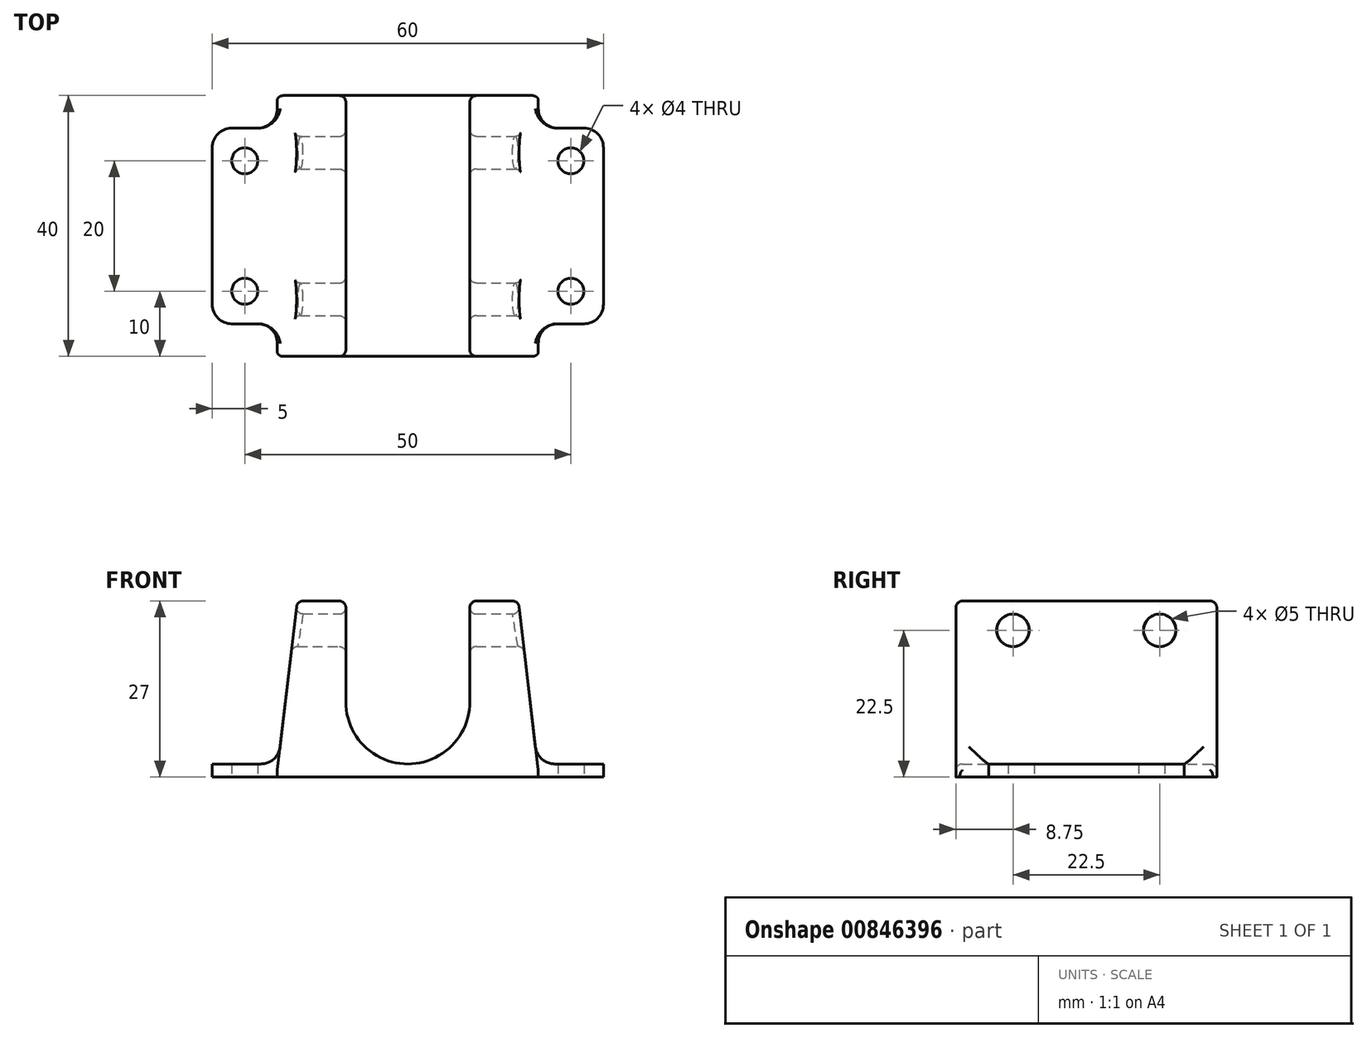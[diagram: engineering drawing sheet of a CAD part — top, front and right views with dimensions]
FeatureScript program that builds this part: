
annotation { "Feature Type Name" : "Feature", "Feature Type Description" : "" }
export const myFeature = defineFeature(function(context is Context, id is Id, definition is map)
    precondition{}
    {
        {
            var Q0;
            Q0=qCreatedBy(makeId("Front.planeOp"),FACE);
            var sketch = newSketch(context, id + "F0", { "sketchPlane" : qUnion([Q0])});
            skLineSegment(sketch, "E0.bottom", {"start": v(0, 0) * mm, "end": v(-20, 0) * mm});
            skLineSegment(sketch, "E0.right", {"start": v(-20, 0) * mm, "end": v(-20, 1) * mm});
            skArc(sketch, "E1", {"start": v(-9.5, 11.56) * mm, "mid": v(-6.74, 4.8) * mm, "end": v(0, 2) * mm});
            skLineSegment(sketch, "E2", {"start": v(-16.95, 27) * mm, "end": v(-20, 1) * mm});
            skLineSegment(sketch, "E3", {"start": v(-9.5, 11.56) * mm, "end": v(-9.5, 27) * mm});
            skPoint(sketch, "E4.end.orphan", {"position": v(-10, 27) * mm});
            skLineSegment(sketch, "E5", {"start": v(-16.95, 27) * mm, "end": v(-9.5, 27) * mm});
            skLineSegment(sketch, "E6.MirrorCS", {"start": v(16.95, 27) * mm, "end": v(20, 1) * mm});
            skLineSegment(sketch, "E7.MirrorCS", {"start": v(16.95, 27) * mm, "end": v(9.5, 27) * mm});
            skLineSegment(sketch, "E8.MirrorCS", {"start": v(9.5, 11.56) * mm, "end": v(9.5, 27) * mm});
            skArc(sketch, "E9.MirrorCS", {"start": v(9.5, 11.56) * mm, "mid": v(6.74, 4.8) * mm, "end": v(0, 2) * mm});
            skLineSegment(sketch, "E10.MirrorCS", {"start": v(0, 0) * mm, "end": v(20, 0) * mm});
            skLineSegment(sketch, "E11.MirrorCS", {"start": v(20, 0) * mm, "end": v(20, 1) * mm});
            skSolve(sketch);
        }
        {
            var Q0;
            Q0 = qSketchRegion(id + "F0", true);
            extrude(context, id + "F1", {"entities" : qUnion([Q0]), "endBound" : BoundingType.SYMMETRIC, "depth" : 40 * mm, "offsetDistance" : 25 * mm});
        }
        {
            var Q0;
            Q0=qCreatedBy(makeId("Right.planeOp"),FACE);
            var sketch = newSketch(context, id + "F2", { "sketchPlane" : qUnion([Q0])});
            skCircle(sketch, "E12", {"center": v(11.25, 22.5) * mm, "radius": 2.5 * mm});
            skCircle(sketch, "E13", {"center": v(-11.25, 22.5) * mm, "radius": 2.5 * mm});
            skSolve(sketch);
        }
        {
            var Q0;
            Q0 = qSketchRegion(id + "F2", true);
            extrude(context, id + "F3", {"entities" : qUnion([Q0]), "operationType" : NewBodyOperationType.REMOVE, "endBound" : BoundingType.SYMMETRIC, "oppositeDirection" : true, "depth" : 40 * mm, "offsetDistance" : 25 * mm});
        }
        {
            var Q0;
            Q0=makeQuery(id+"F1.opExtrude","SWEPT_FACE",FACE,{"disambiguationData":[OSD([sQuery(id+"F0.wireOp",EDGE,"E5")])]});
            var Q1;
            Q1=makeQuery(id+"F1.opExtrude","SWEPT_FACE",FACE,{"disambiguationData":[OSD([sQuery(id+"F0.wireOp",EDGE,"E7.MirrorCS")])]});
            var Q2;
            Q2=makeQuery(id+"F1.opExtrude","CAP_EDGE",EDGE,{"disambiguationData":[OSD([sQuery(id+"F0.wireOp",EDGE,"E6.MirrorCS")])],"isStart":false});
            var Q3;
            Q3=makeQuery(id+"F1.opExtrude","CAP_EDGE",EDGE,{"disambiguationData":[OSD([sQuery(id+"F0.wireOp",EDGE,"E6.MirrorCS")])],"isStart":true});
            var Q4;
            Q4=makeQuery(id+"F1.opExtrude","CAP_EDGE",EDGE,{"disambiguationData":[OSD([sQuery(id+"F0.wireOp",EDGE,"E2")])],"isStart":true});
            var Q5;
            Q5=makeQuery(id+"F1.opExtrude","CAP_EDGE",EDGE,{"disambiguationData":[OSD([sQuery(id+"F0.wireOp",EDGE,"E2")])],"isStart":false});
            var Q6;
            Q6=makeQuery(id+"F1.opExtrude","SWEPT_FACE",FACE,{"disambiguationData":[OSD([sQuery(id+"F0.wireOp",EDGE,"E1"),sQuery(id+"F0.wireOp",EDGE,"E9.MirrorCS")])]});
            var Q7;
            Q7=makeQuery(id+"F1.opExtrude","SWEPT_FACE",FACE,{"disambiguationData":[OSD([sQuery(id+"F0.wireOp",EDGE,"E8.MirrorCS")])]});
            var Q8;
            Q8=makeQuery(id+"F1.opExtrude","SWEPT_FACE",FACE,{"disambiguationData":[OSD([sQuery(id+"F0.wireOp",EDGE,"E3")])]});
            var Q9;
            Q9=makeQuery(id+"F1.opExtrude","SWEPT_FACE",FACE,{"disambiguationData":[OSD([sQuery(id+"F0.wireOp",EDGE,"E2")])]});
            var Q10;
            Q10=makeQuery(id+"F1.opExtrude","SWEPT_FACE",FACE,{"disambiguationData":[OSD([sQuery(id+"F0.wireOp",EDGE,"E6.MirrorCS")])]});
            fillet(context, id + "F4", {"entities" : qUnion([Q0, Q1, Q2, Q3, Q4, Q5, Q6, Q7, Q8, Q9, Q10]), "radius" : 1 * mm, "tangentPropagation" : true, "allowEdgeOverflow" : false});
        }
        {
            var Q0;
            Q0=makeQuery(id+"F1.opExtrude","SWEPT_FACE",FACE,{"disambiguationData":[OSD([sQuery(id+"F0.wireOp",EDGE,"E0.bottom"),sQuery(id+"F0.wireOp",EDGE,"E10.MirrorCS")])]});
            var sketch = newSketch(context, id + "F5", { "sketchPlane" : qUnion([Q0])});
            skLineSegment(sketch, "E14.bottom", {"start": v(-30, 15) * mm, "end": v(30, 15) * mm});
            skLineSegment(sketch, "E14.top", {"start": v(-30, -15) * mm, "end": v(30, -15) * mm});
            skLineSegment(sketch, "E14.left", {"start": v(-30, 15) * mm, "end": v(-30, -15) * mm});
            skLineSegment(sketch, "E14.right", {"start": v(30, 15) * mm, "end": v(30, -15) * mm});
            skCircle(sketch, "E15", {"center": v(-25, 10) * mm, "radius": 2 * mm});
            skCircle(sketch, "E16.0.1.0", {"center": v(-25, -10) * mm, "radius": 2 * mm});
            skCircle(sketch, "E16.1.0.0", {"center": v(25, 10) * mm, "radius": 2 * mm});
            skCircle(sketch, "E16.1.1.0", {"center": v(25, -10) * mm, "radius": 2 * mm});
            skLineSegment(sketch, "E16.direction1", {"start": v(-25, 10) * mm, "end": v(25, 10) * mm, "construction": true});
            skLineSegment(sketch, "E16.direction2", {"start": v(-25, 10) * mm, "end": v(-25, -10) * mm, "construction": true});
            skSolve(sketch);
        }
        {
            var Q0;
            Q0 = qSketchRegion(id + "F5", true);
            extrude(context, id + "F6", {"entities" : qUnion([Q0]), "operationType" : NewBodyOperationType.ADD, "oppositeDirection" : true, "depth" : 2 * mm, "offsetDistance" : 25 * mm});
        }
        {
            var Q0;
            Q0=makeQuery(id+"F6.boolean.opBoolean","INTERSECT",EDGE,{"derivedFrom":[makeQuery(id+"F1.opExtrude","SWEPT_FACE",FACE,{"disambiguationData":[OSD([sQuery(id+"F0.wireOp",EDGE,"E2")])]}),makeQuery(id+"F6.opExtrude","CAP_FACE",FACE,{"disambiguationData":[OSD([sQuery(id+"F5.wireOp",EDGE,"E14.bottom"),sQuery(id+"F5.wireOp",EDGE,"E14.top"),sQuery(id+"F5.wireOp",EDGE,"E14.left"),sQuery(id+"F5.wireOp",EDGE,"E14.right"),sQuery(id+"F5.wireOp",EDGE,"E15"),sQuery(id+"F5.wireOp",EDGE,"E16.0.1.0"),sQuery(id+"F5.wireOp",EDGE,"E16.1.0.0"),sQuery(id+"F5.wireOp",EDGE,"E16.1.1.0")])],"isStart":false})]});
            var Q1;
            Q1=makeQuery(id+"F6.boolean.opBoolean","INTERSECT",EDGE,{"derivedFrom":[makeQuery(id+"F1.opExtrude","SWEPT_FACE",FACE,{"disambiguationData":[OSD([sQuery(id+"F0.wireOp",EDGE,"E2")])]}),makeQuery(id+"F6.opExtrude","SWEPT_FACE",FACE,{"disambiguationData":[OSD([sQuery(id+"F5.wireOp",EDGE,"E14.top")])]})]});
            var Q2;
            Q2=makeQuery(id+"F6.boolean.opBoolean","INTERSECT",EDGE,{"derivedFrom":[makeQuery(id+"F1.opExtrude","SWEPT_FACE",FACE,{"disambiguationData":[OSD([sQuery(id+"F0.wireOp",EDGE,"E2")])]}),makeQuery(id+"F6.opExtrude","SWEPT_FACE",FACE,{"disambiguationData":[OSD([sQuery(id+"F5.wireOp",EDGE,"E14.bottom")])]})]});
            var Q3;
            Q3=makeQuery(id+"F6.opExtrude","SWEPT_EDGE",EDGE,{"disambiguationData":[OSD([sQuery(id+"F5.wireOp",EDGE,"E14.bottom"),sQuery(id+"F5.wireOp",EDGE,"E14.left")])]});
            var Q4;
            Q4=makeQuery(id+"F6.opExtrude","SWEPT_EDGE",EDGE,{"disambiguationData":[OSD([sQuery(id+"F5.wireOp",EDGE,"E14.top"),sQuery(id+"F5.wireOp",EDGE,"E14.left")])]});
            var Q5;
            Q5=makeQuery(id+"F6.boolean.opBoolean","INTERSECT",EDGE,{"derivedFrom":[makeQuery(id+"F1.opExtrude","SWEPT_FACE",FACE,{"disambiguationData":[OSD([sQuery(id+"F0.wireOp",EDGE,"E6.MirrorCS")])]}),makeQuery(id+"F6.opExtrude","CAP_FACE",FACE,{"disambiguationData":[OSD([sQuery(id+"F5.wireOp",EDGE,"E14.bottom"),sQuery(id+"F5.wireOp",EDGE,"E14.top"),sQuery(id+"F5.wireOp",EDGE,"E14.left"),sQuery(id+"F5.wireOp",EDGE,"E14.right"),sQuery(id+"F5.wireOp",EDGE,"E15"),sQuery(id+"F5.wireOp",EDGE,"E16.0.1.0"),sQuery(id+"F5.wireOp",EDGE,"E16.1.0.0"),sQuery(id+"F5.wireOp",EDGE,"E16.1.1.0")])],"isStart":false})]});
            var Q6;
            Q6=makeQuery(id+"F6.boolean.opBoolean","INTERSECT",EDGE,{"derivedFrom":[makeQuery(id+"F1.opExtrude","SWEPT_FACE",FACE,{"disambiguationData":[OSD([sQuery(id+"F0.wireOp",EDGE,"E6.MirrorCS")])]}),makeQuery(id+"F6.opExtrude","SWEPT_FACE",FACE,{"disambiguationData":[OSD([sQuery(id+"F5.wireOp",EDGE,"E14.bottom")])]})]});
            var Q7;
            Q7=makeQuery(id+"F6.boolean.opBoolean","INTERSECT",EDGE,{"derivedFrom":[makeQuery(id+"F1.opExtrude","SWEPT_FACE",FACE,{"disambiguationData":[OSD([sQuery(id+"F0.wireOp",EDGE,"E6.MirrorCS")])]}),makeQuery(id+"F6.opExtrude","SWEPT_FACE",FACE,{"disambiguationData":[OSD([sQuery(id+"F5.wireOp",EDGE,"E14.top")])]})]});
            var Q8;
            Q8=makeQuery(id+"F6.opExtrude","SWEPT_EDGE",EDGE,{"disambiguationData":[OSD([sQuery(id+"F5.wireOp",EDGE,"E14.top"),sQuery(id+"F5.wireOp",EDGE,"E14.right")])]});
            var Q9;
            Q9=makeQuery(id+"F6.opExtrude","SWEPT_EDGE",EDGE,{"disambiguationData":[OSD([sQuery(id+"F5.wireOp",EDGE,"E14.bottom"),sQuery(id+"F5.wireOp",EDGE,"E14.right")])]});
            fillet(context, id + "F7", {"entities" : qUnion([Q0, Q1, Q2, Q3, Q4, Q5, Q6, Q7, Q8, Q9]), "tangentPropagation" : true, "radius" : 3 * mm, "defaultsChanged" : false, "vertexSettings" : [], "allowEdgeOverflow" : false});
        }
    });
